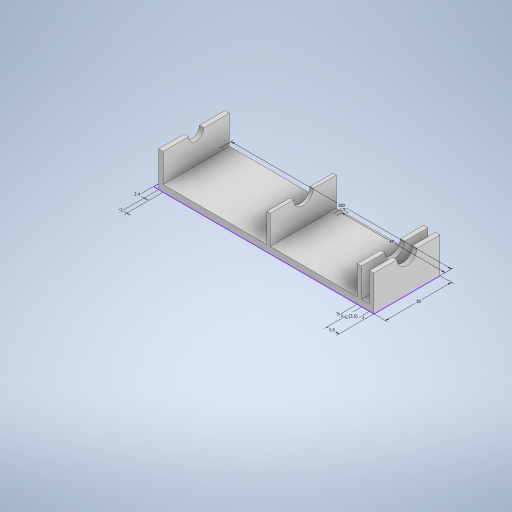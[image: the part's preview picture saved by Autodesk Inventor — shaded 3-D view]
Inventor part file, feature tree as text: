
AUTODESK INVENTOR PART (.ipt)
format: ipt  version: 2023.2 (Build 272271000, 271)  size: 645,632 bytes
history: native  units: mm
features: extrude x8, sketch x3, projected_geometry x1
ambient origin geometry x8: Origin, YZ Plane, XZ Plane, XY Plane, X Axis, Y Axis, Z Axis, Center Point
bodies: Solid1 (feature_tree)
feature tree (12):
  sketch  "Sketch1"  dims[d0=100.0mm d1=30.0mm]
  extrude  "Extrusion1"  Depth=30.0mm
  extrude  "Extrusion2"  Depth=2.0mm
  extrude  "Extrusion8"  Depth=2.0mm
  extrude  "Extrusion4"  Depth=3.0mm TaperAngle=0.0deg
  extrude  "Extrusion5"  Depth=16.0mm TaperAngle=0.0deg
  extrude  "Extrusion9"  Depth=16.0mm TaperAngle=0.0deg
  extrude  "Extrusion6"  Depth=3.0mm TaperAngle=0.0deg
  extrude  "Extrusion7"  Depth=3.0mm TaperAngle=0.0deg
  sketch  "Sketch2"  dims[d2=2.4mm d3=2.0mm]
  projected_geometry  "Projected Loop1"
  sketch  "Sketch3"  dims[d4=5.5mm d5=2.0mm d6=3.0mm d7=0.0mm d8=16.0mm d9=0.0mm d12=16.0mm d13=0.0mm d14=3.0mm d15=0.0mm d16=3.0mm d17=0.0mm d18=9.0mm d19=7.0mm d20=10.0mm d21=0.0mm d24=47.0mm d25=1.5mm d26=16.0mm d27=0.0mm d28=2.0mm d29=3.5mm d30=16.0mm d31=0.0mm d22=0.872665mm]
